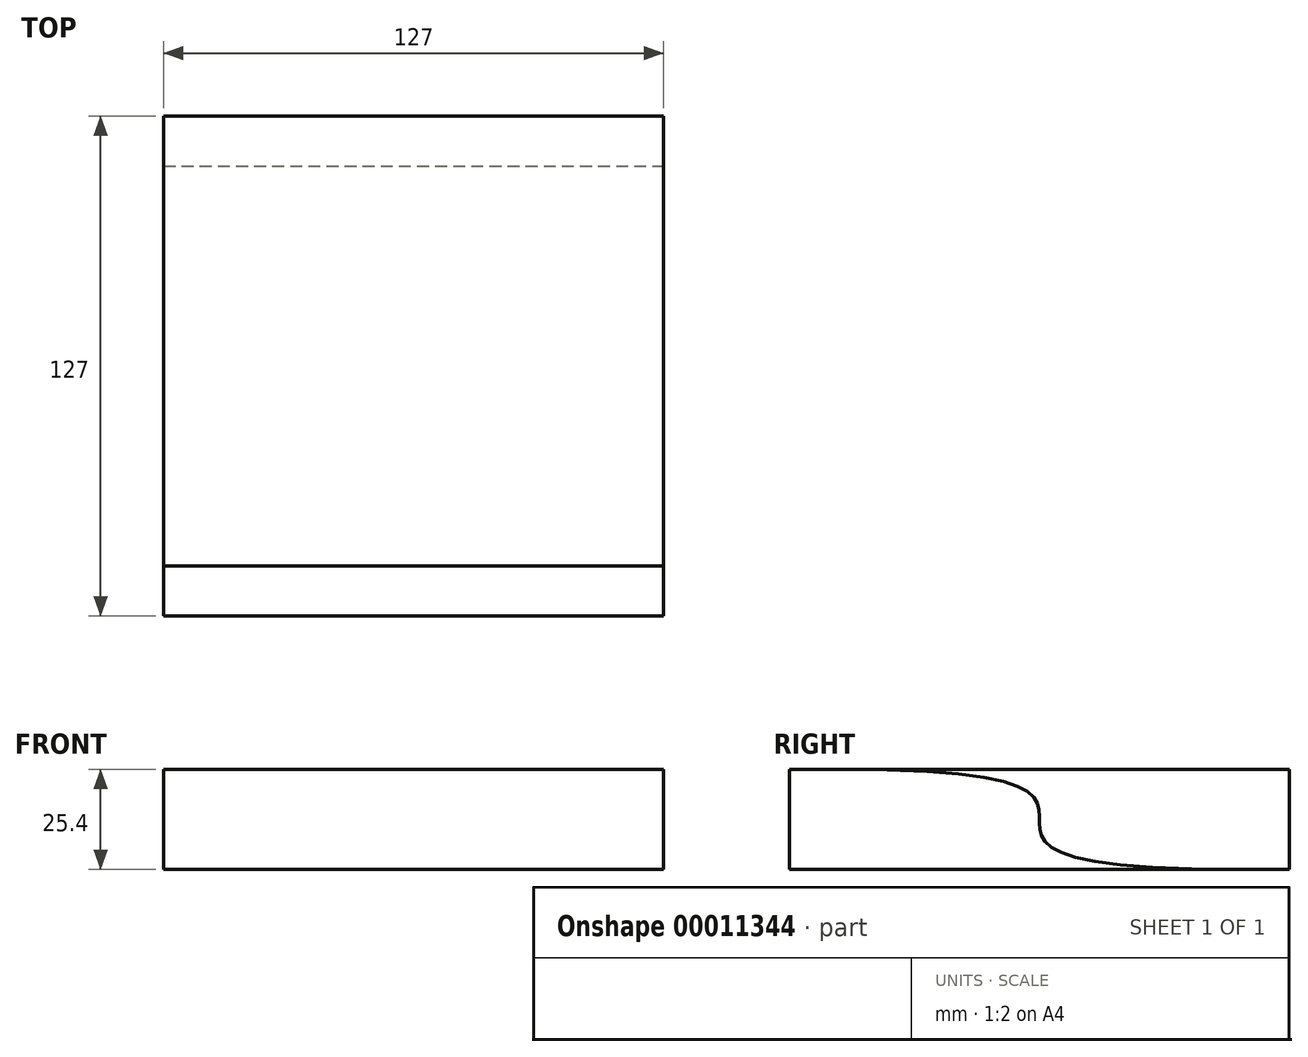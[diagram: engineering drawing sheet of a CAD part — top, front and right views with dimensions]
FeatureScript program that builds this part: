
annotation { "Feature Type Name" : "Feature", "Feature Type Description" : "" }
export const myFeature = defineFeature(function(context is Context, id is Id, definition is map)
    precondition{}
    {
        {
            var Q0;
            Q0=qCreatedBy(makeId("Top.planeOp"),FACE);
            var sketch = newSketch(context, id + "F0", { "sketchPlane" : qUnion([Q0])});
            skLineSegment(sketch, "E0.rect.bottom", {"start": v(-63.5, 63.5) * mm, "end": v(63.5, 63.5) * mm});
            skLineSegment(sketch, "E0.rect.top", {"start": v(-63.5, -63.5) * mm, "end": v(63.5, -63.5) * mm});
            skLineSegment(sketch, "E0.rect.left", {"start": v(-63.5, 63.5) * mm, "end": v(-63.5, -63.5) * mm});
            skLineSegment(sketch, "E0.rect.right", {"start": v(63.5, 63.5) * mm, "end": v(63.5, -63.5) * mm});
            skPoint(sketch, "E0.rect.middle", {"position": v(0, 0) * mm});
            skSolve(sketch);
        }
        {
            var Q0;
            Q0=makeQuery(id+"F0.imprint","IMPRINT",FACE,{"disambiguationData":[TD([[makeQuery(id+"F0.imprint","IMPRINT",EDGE,{"derivedFrom":sQuery(id+"F0.wireOp",EDGE,"E0.rect.bottom")}),-1.0]])]});
            extrude(context, id + "F1", {"entities" : qUnion([Q0]), "depth" : 25.4 * mm});
        }
        {
            var Q0;
            Q0=makeQuery(id+"F1.opExtrude","SWEPT_FACE",FACE,{"disambiguationData":[OSD([sQuery(id+"F0.wireOp",EDGE,"E0.rect.right")])]});
            var sketch = newSketch(context, id + "F2", { "sketchPlane" : qUnion([Q0])});
            skFitSpline(sketch, "E1", {"points": [v(-50.8, 25.4) * mm, v(0, 12.7) * mm, v(50.8, 0) * mm], "startDerivative": vector(304.8, 0) * mm, "endDerivative": vector(304.8, 0) * mm});
            skPoint(sketch, "E2", {"position": v(-63.5, 12.7) * mm});
            skSolve(sketch);
        }
        {
            var Q0;
            Q0 = qSketchRegion(id + "F2", true);
            var Q1;
            {var subQ2=sQuery(id+"F2.wireOp",EDGE,"E1");Q1=makeQuery(id+"F2.imprint","IMPRINT",FACE,{"disambiguationData":[TD([[makeQuery(id+"F2.imprint","IMPRINT",EDGE,{"derivedFrom":subQ2}),1.0]])]});}
            extrude(context, id + "F3", {"entities" : qUnion([Q0, Q1]), "operationType" : NewBodyOperationType.REMOVE, "endBound" : BoundingType.THROUGH_ALL, "oppositeDirection" : true, "depth" : 25.4 * mm});
        }
        {
            var Q0;
            Q0=makeQuery(id+"F1.opExtrude","SWEPT_FACE",FACE,{"disambiguationData":[OSD([sQuery(id+"F0.wireOp",EDGE,"E0.rect.right")])]});
            var sketch = newSketch(context, id + "F4", { "sketchPlane" : qUnion([Q0])});
            skLineSegment(sketch, "E3", {"start": v(-50.8, 25.4) * mm, "end": v(63.5, 25.4) * mm});
            skLineSegment(sketch, "E4", {"start": v(63.5, 25.4) * mm, "end": v(63.5, 0) * mm});
            skLineSegment(sketch, "E5", {"start": v(63.5, 0) * mm, "end": v(50.8, 0) * mm});
            skFitSpline(sketch, "E6", {"points": [v(-50.8, 25.4) * mm, v(0, 12.7) * mm, v(50.8, 0) * mm], "startDerivative": vector(304.8, 0) * mm, "endDerivative": vector(304.8, 0) * mm});
            skPoint(sketch, "E7", {"position": v(63.5, 12.7) * mm});
            skSolve(sketch);
        }
        {
            var Q0;
            Q0=makeQuery(id+"F4.imprint","IMPRINT",FACE,{"disambiguationData":[TD([[makeQuery(id+"F4.imprint","IMPRINT",EDGE,{"derivedFrom":sQuery(id+"F4.wireOp",EDGE,"E3")}),-1.0]])]});
            var Q1;
            Q1=makeQuery(id+"F1.opExtrude","SWEPT_FACE",FACE,{"disambiguationData":[OSD([sQuery(id+"F0.wireOp",EDGE,"E0.rect.left")])]});
            extrude(context, id + "F5", {"entities" : qUnion([Q0]), "endBound" : BoundingType.UP_TO_SURFACE, "oppositeDirection" : true, "endBoundEntityFace" : qUnion([Q1]), "depth" : 25.4 * mm});
        }
    });
